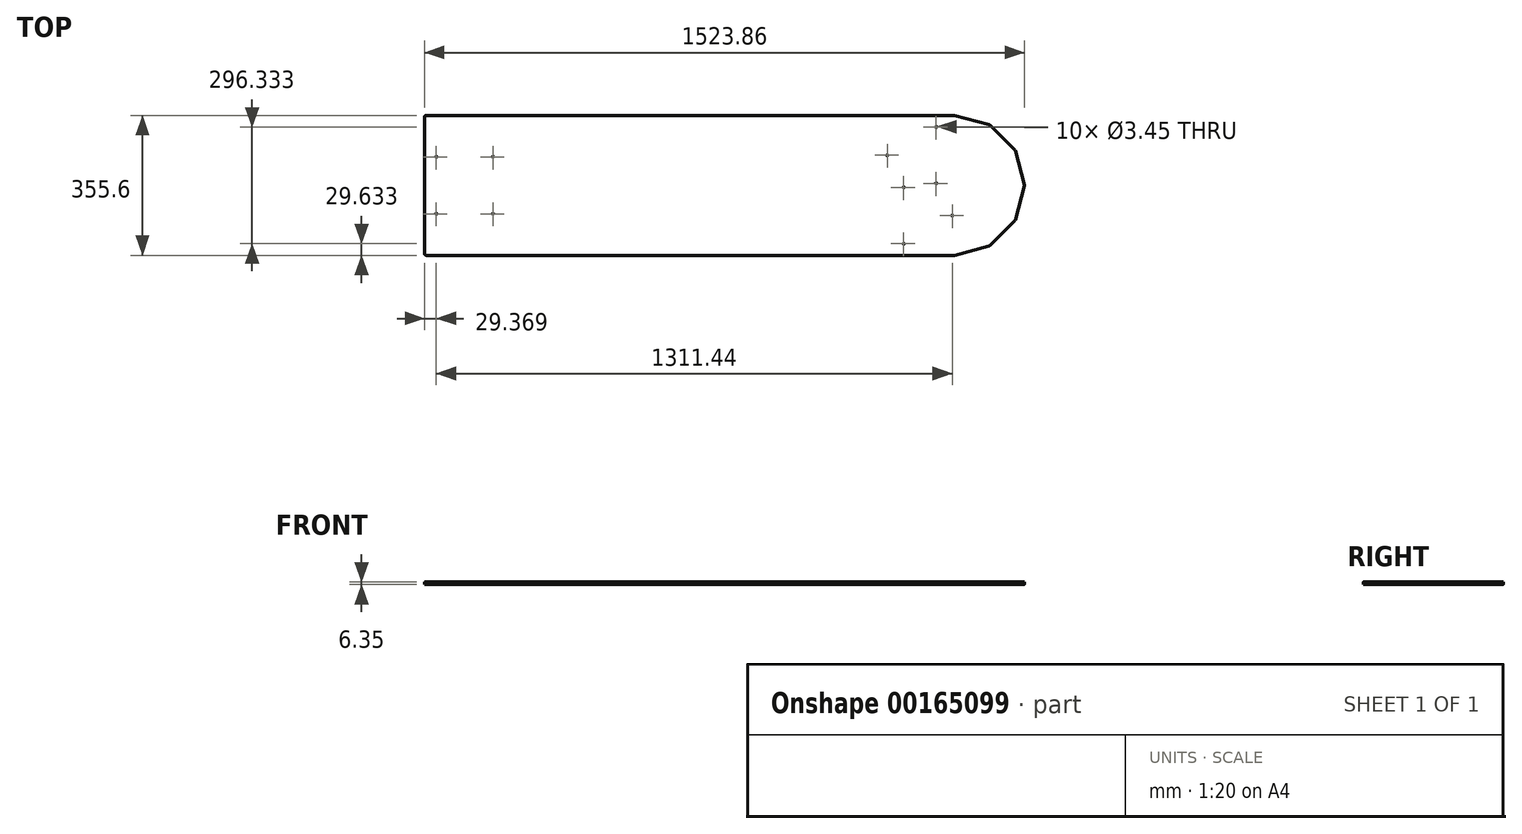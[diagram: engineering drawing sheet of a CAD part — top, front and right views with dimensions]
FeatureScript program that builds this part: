
annotation { "Feature Type Name" : "Feature", "Feature Type Description" : "" }
export const myFeature = defineFeature(function(context is Context, id is Id, definition is map)
    precondition{}
    {
        {
            var Q0;
            Q0=qCreatedBy(makeId("Top.planeOp"),FACE);
            var sketch = newSketch(context, id + "F0", { "sketchPlane" : qUnion([Q0])});
            skLineSegment(sketch, "E0", {"start": v(0, 0) * mm, "end": v(0, -177.8) * mm, "construction": true});
            skLineSegment(sketch, "E1", {"start": v(0, 0) * mm, "end": v(88.9, -153.98) * mm, "construction": true});
            skLineSegment(sketch, "E2", {"start": v(0, 0) * mm, "end": v(153.98, -88.9) * mm, "construction": true});
            skLineSegment(sketch, "E3", {"start": v(0, 0) * mm, "end": v(177.8, 0) * mm, "construction": true});
            skLineSegment(sketch, "E4", {"start": v(0, 0) * mm, "end": v(0, 177.8) * mm, "construction": true});
            skLineSegment(sketch, "E5", {"start": v(0, 0) * mm, "end": v(88.9, 153.98) * mm, "construction": true});
            skLineSegment(sketch, "E6", {"start": v(0, 0) * mm, "end": v(153.98, 88.9) * mm, "construction": true});
            skLineSegment(sketch, "E7", {"start": v(0, 177.8) * mm, "end": v(88.9, 153.98) * mm});
            skLineSegment(sketch, "E8", {"start": v(88.9, 153.98) * mm, "end": v(153.98, 88.9) * mm});
            skLineSegment(sketch, "E9", {"start": v(153.98, 88.9) * mm, "end": v(177.8, 0) * mm});
            skLineSegment(sketch, "E10", {"start": v(177.8, 0) * mm, "end": v(153.98, -88.9) * mm});
            skLineSegment(sketch, "E11", {"start": v(153.98, -88.9) * mm, "end": v(88.9, -153.98) * mm});
            skLineSegment(sketch, "E12", {"start": v(88.9, -153.98) * mm, "end": v(0, -177.8) * mm});
            skLineSegment(sketch, "E13", {"start": v(0, 177.8) * mm, "end": v(-1346.2, 177.8) * mm});
            skLineSegment(sketch, "E14", {"start": v(-1346.2, 177.8) * mm, "end": v(-1346.2, -177.8) * mm});
            skLineSegment(sketch, "E15", {"start": v(-1346.2, -177.8) * mm, "end": v(0, -177.8) * mm});
            skLineSegment(sketch, "E16", {"start": v(-1346.2, 0) * mm, "end": v(-1244.6, 0) * mm, "construction": true});
            skLineSegment(sketch, "E17.bottom", {"start": v(-1316.83, -72.23) * mm, "end": v(-1172.37, -72.23) * mm, "construction": true});
            skLineSegment(sketch, "E17.top", {"start": v(-1316.83, 72.23) * mm, "end": v(-1172.37, 72.23) * mm, "construction": true});
            skLineSegment(sketch, "E17.left", {"start": v(-1316.83, -72.23) * mm, "end": v(-1316.83, 72.23) * mm, "construction": true});
            skLineSegment(sketch, "E17.right", {"start": v(-1172.37, -72.23) * mm, "end": v(-1172.37, 72.23) * mm, "construction": true});
            skPoint(sketch, "E17.middle", {"position": v(-1244.6, 0) * mm});
            skCircle(sketch, "E18", {"center": v(-1172.37, 72.23) * mm, "radius": 1.73 * mm});
            skCircle(sketch, "E19", {"center": v(-1316.83, 72.23) * mm, "radius": 1.73 * mm});
            skCircle(sketch, "E20", {"center": v(-1316.83, -72.23) * mm, "radius": 1.73 * mm});
            skCircle(sketch, "E21", {"center": v(-1172.37, -72.23) * mm, "radius": 1.73 * mm});
            skLineSegment(sketch, "E22", {"start": v(0, 0) * mm, "end": v(-87.94, 0) * mm, "construction": true});
            skLineSegment(sketch, "E23", {"start": v(-87.94, 76.68) * mm, "end": v(-87.94, -76.68) * mm, "construction": true});
            skLineSegment(sketch, "E24", {"start": v(-673.1, 177.8) * mm, "end": v(-673.1, 152.4) * mm, "construction": true});
            skLineSegment(sketch, "E25", {"start": v(-1346.2, 152.4) * mm, "end": v(0, 152.4) * mm, "construction": true});
            skLineSegment(sketch, "E26", {"start": v(-87.94, 76.68) * mm, "end": v(-170.49, 76.68) * mm, "construction": true});
            skLineSegment(sketch, "E27", {"start": v(-170.49, 76.68) * mm, "end": v(-46.66, 148.17) * mm, "construction": true});
            skLineSegment(sketch, "E28", {"start": v(-46.66, 148.17) * mm, "end": v(-87.94, 76.68) * mm, "construction": true});
            skLineSegment(sketch, "E29", {"start": v(-170.49, 76.68) * mm, "end": v(-46.66, 5.19) * mm, "construction": true});
            skLineSegment(sketch, "E30", {"start": v(-46.66, 5.19) * mm, "end": v(-87.94, 76.68) * mm, "construction": true});
            skLineSegment(sketch, "E31", {"start": v(-46.66, 5.19) * mm, "end": v(-46.66, 148.17) * mm, "construction": true});
            skLineSegment(sketch, "E32", {"start": v(-129.21, -5.19) * mm, "end": v(-129.21, -148.17) * mm, "construction": true});
            skLineSegment(sketch, "E33", {"start": v(-129.21, -148.17) * mm, "end": v(-87.94, -76.68) * mm, "construction": true});
            skLineSegment(sketch, "E34", {"start": v(-87.94, -76.68) * mm, "end": v(-5.39, -76.68) * mm, "construction": true});
            skLineSegment(sketch, "E35", {"start": v(-5.39, -76.68) * mm, "end": v(-129.21, -5.19) * mm, "construction": true});
            skLineSegment(sketch, "E36", {"start": v(-129.21, -5.19) * mm, "end": v(-87.94, -76.68) * mm, "construction": true});
            skLineSegment(sketch, "E37", {"start": v(-5.39, -76.68) * mm, "end": v(-129.21, -148.17) * mm, "construction": true});
            skCircle(sketch, "E38", {"center": v(-46.66, 148.17) * mm, "radius": 4.23 * mm, "construction": true});
            skLineSegment(sketch, "E39", {"start": v(75.75, 131.2) * mm, "end": v(0, 151.5) * mm, "construction": true});
            skLineSegment(sketch, "E40", {"start": v(75.75, 131.2) * mm, "end": v(133.16, 76.88) * mm, "construction": true});
            skLineSegment(sketch, "E41", {"start": v(37.88, 141.36) * mm, "end": v(44.45, 165.89) * mm, "construction": true});
            skCircle(sketch, "E42", {"center": v(-170.49, 76.68) * mm, "radius": 1.73 * mm});
            skCircle(sketch, "E43", {"center": v(-46.66, 5.19) * mm, "radius": 1.73 * mm});
            skCircle(sketch, "E44", {"center": v(-5.39, -76.68) * mm, "radius": 1.73 * mm});
            skCircle(sketch, "E45", {"center": v(-129.21, -148.17) * mm, "radius": 1.73 * mm});
            skCircle(sketch, "E46", {"center": v(-129.21, -5.19) * mm, "radius": 1.73 * mm});
            skCircle(sketch, "E47", {"center": v(-46.66, 148.17) * mm, "radius": 1.73 * mm});
            skSolve(sketch);
        }
        {
            var Q0;
            Q0=makeQuery(id+"F0.imprint","IMPRINT",FACE,{"disambiguationData":[TD([[makeQuery(id+"F0.imprint","IMPRINT",EDGE,{"derivedFrom":sQuery(id+"F0.wireOp",EDGE,"E7")}),-1.0]])]});
            extrude(context, id + "F1", {"entities" : qUnion([Q0]), "depth" : 6.35 * mm});
        }
        {
            var Q0;
            Q0=makeQuery(id+"F1.opExtrude","SWEPT_EDGE",EDGE,{"disambiguationData":[OSD([sQuery(id+"F0.wireOp",EDGE,"E12"),sQuery(id+"F0.wireOp",EDGE,"E15")])]});
            var Q1;
            Q1=makeQuery(id+"F1.opExtrude","SWEPT_EDGE",EDGE,{"disambiguationData":[OSD([sQuery(id+"F0.wireOp",EDGE,"E11"),sQuery(id+"F0.wireOp",EDGE,"E12")])]});
            var Q2;
            Q2=makeQuery(id+"F1.opExtrude","SWEPT_EDGE",EDGE,{"disambiguationData":[OSD([sQuery(id+"F0.wireOp",EDGE,"E10"),sQuery(id+"F0.wireOp",EDGE,"E11")])]});
            var Q3;
            Q3=makeQuery(id+"F1.opExtrude","SWEPT_EDGE",EDGE,{"disambiguationData":[OSD([sQuery(id+"F0.wireOp",EDGE,"E9"),sQuery(id+"F0.wireOp",EDGE,"E10")])]});
            var Q4;
            Q4=makeQuery(id+"F1.opExtrude","SWEPT_EDGE",EDGE,{"disambiguationData":[OSD([sQuery(id+"F0.wireOp",EDGE,"E8"),sQuery(id+"F0.wireOp",EDGE,"E9")])]});
            var Q5;
            Q5=makeQuery(id+"F1.opExtrude","SWEPT_EDGE",EDGE,{"disambiguationData":[OSD([sQuery(id+"F0.wireOp",EDGE,"E7"),sQuery(id+"F0.wireOp",EDGE,"E8")])]});
            var Q6;
            Q6=makeQuery(id+"F1.opExtrude","SWEPT_EDGE",EDGE,{"disambiguationData":[OSD([sQuery(id+"F0.wireOp",EDGE,"E7"),sQuery(id+"F0.wireOp",EDGE,"E13")])]});
            var Q7;
            Q7=makeQuery(id+"F1.opExtrude","SWEPT_EDGE",EDGE,{"disambiguationData":[OSD([sQuery(id+"F0.wireOp",EDGE,"E13"),sQuery(id+"F0.wireOp",EDGE,"E14")])]});
            var Q8;
            Q8=makeQuery(id+"F1.opExtrude","SWEPT_EDGE",EDGE,{"disambiguationData":[OSD([sQuery(id+"F0.wireOp",EDGE,"E14"),sQuery(id+"F0.wireOp",EDGE,"E15")])]});
            fillet(context, id + "F2", {"entities" : qUnion([Q0, Q1, Q2, Q3, Q4, Q5, Q6, Q7, Q8]), "radius" : 3.97 * mm, "tangentPropagation" : true, "allowEdgeOverflow" : false});
        }
    });
